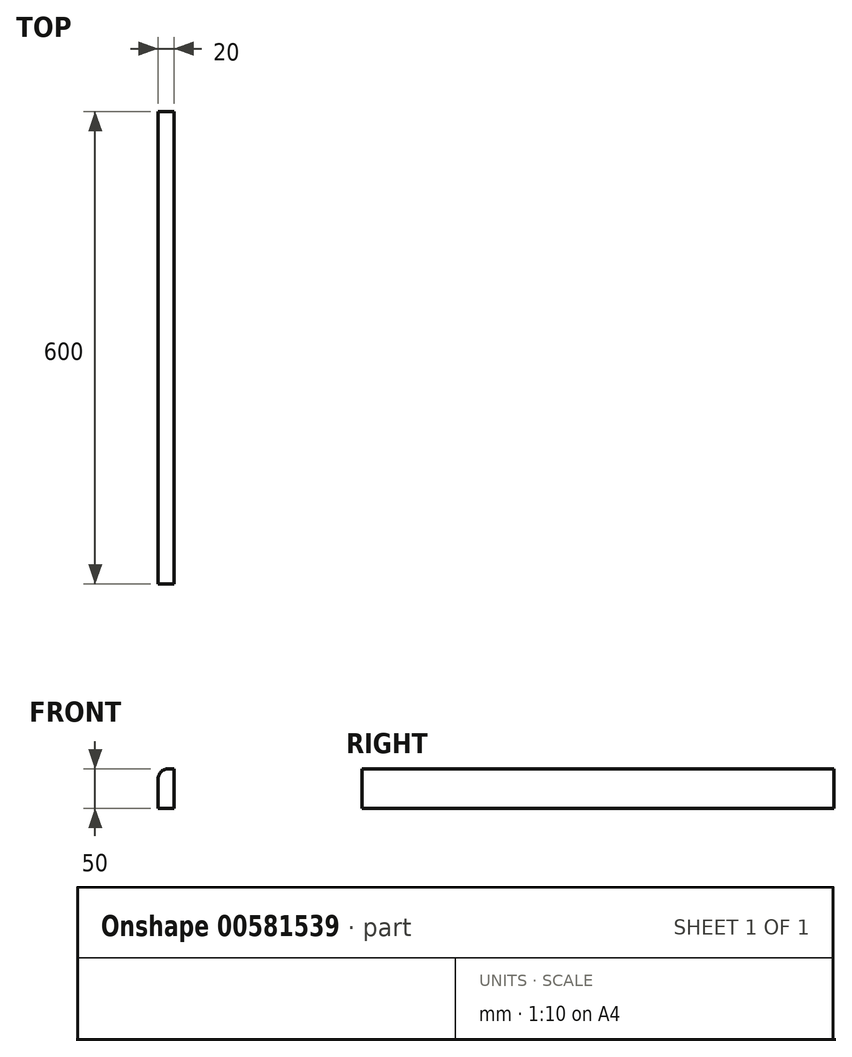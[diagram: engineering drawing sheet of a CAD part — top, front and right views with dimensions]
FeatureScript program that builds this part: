
annotation { "Feature Type Name" : "Feature", "Feature Type Description" : "" }
export const myFeature = defineFeature(function(context is Context, id is Id, definition is map)
    precondition{}
    {
        {
            var Q0;
            Q0=qCreatedBy(makeId("Top.planeOp"),FACE);
            var sketch = newSketch(context, id + "F0", { "sketchPlane" : qUnion([Q0])});
            skLineSegment(sketch, "E0.bottom", {"start": v(-19.69, 600) * mm, "end": v(0.31, 600) * mm});
            skLineSegment(sketch, "E0.top", {"start": v(-19.69, 0) * mm, "end": v(0.31, 0) * mm});
            skLineSegment(sketch, "E0.left", {"start": v(-19.69, 600) * mm, "end": v(-19.69, 0) * mm});
            skLineSegment(sketch, "E0.right", {"start": v(0.31, 600) * mm, "end": v(0.31, 0) * mm});
            skSolve(sketch);
        }
        {
            var Q0;
            Q0=makeQuery(id+"F0.imprint","IMPRINT",FACE,{"disambiguationData":[TD([[makeQuery(id+"F0.imprint","IMPRINT",EDGE,{"derivedFrom":sQuery(id+"F0.wireOp",EDGE,"E0.bottom")}),-1.0]])]});
            extrude(context, id + "F1", {"entities" : qUnion([Q0]), "depth" : 50 * mm, "offsetDistance" : 25 * mm});
        }
        {
            var Q0;
            Q0=makeQuery(id+"F1.opExtrude","CAP_EDGE",EDGE,{"disambiguationData":[OSD([sQuery(id+"F0.wireOp",EDGE,"E0.left")])],"isStart":false});
            fillet(context, id + "F2", {"entities" : qUnion([Q0]), "radius" : 12 * mm, "tangentPropagation" : true, "allowEdgeOverflow" : false});
        }
    });
